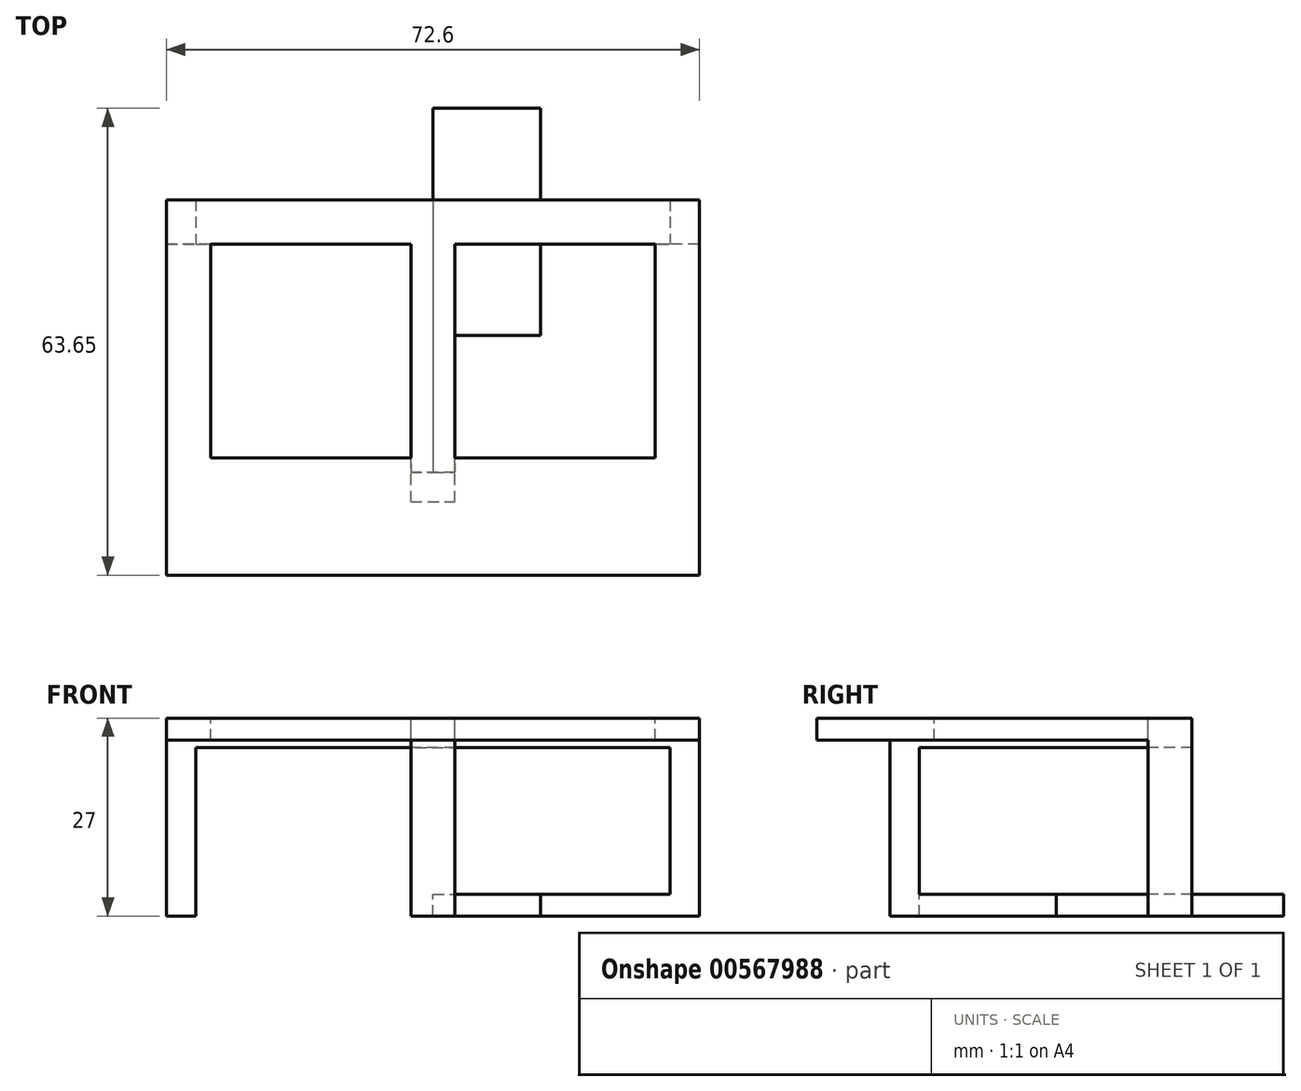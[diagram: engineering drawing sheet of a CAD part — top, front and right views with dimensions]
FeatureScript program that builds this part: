
annotation { "Feature Type Name" : "Feature", "Feature Type Description" : "" }
export const myFeature = defineFeature(function(context is Context, id is Id, definition is map)
    precondition{}
    {
        {
            var Q0;
            Q0=qCreatedBy(makeId("Top.planeOp"),FACE);
            var sketch = newSketch(context, id + "F0", { "sketchPlane" : qUnion([Q0])});
            skLineSegment(sketch, "E0.bottom", {"start": v(-32.12, 30.17) * mm, "end": v(-2.82, 30.17) * mm});
            skLineSegment(sketch, "E0.top", {"start": v(-32.12, -0.83) * mm, "end": v(-2.82, -0.83) * mm});
            skLineSegment(sketch, "E0.left", {"start": v(-32.12, 30.17) * mm, "end": v(-32.12, -0.83) * mm});
            skLineSegment(sketch, "E0.right", {"start": v(-2.82, 30.17) * mm, "end": v(-2.82, -0.83) * mm});
            skSolve(sketch);
        }
        {
            var Q0;
            Q0=makeQuery(id+"F0.imprint","IMPRINT",FACE,{"disambiguationData":[TD([[makeQuery(id+"F0.imprint","IMPRINT",EDGE,{"derivedFrom":sQuery(id+"F0.wireOp",EDGE,"E0.bottom")}),-1.0]])]});
            extrude(context, id + "F1", {"entities" : qUnion([Q0]), "depth" : 3 * mm, "offsetDistance" : 25 * mm});
        }
        {
            var Q0;
            Q0=makeQuery(id+"F1.opExtrude","SWEPT_FACE",FACE,{"disambiguationData":[OSD([sQuery(id+"F0.wireOp",EDGE,"E0.right")])]});
            var sketch = newSketch(context, id + "F2", { "sketchPlane" : qUnion([Q0])});
            skLineSegment(sketch, "E1", {"start": v(17.67, 3) * mm, "end": v(17.67, 0) * mm});
            skLineSegment(sketch, "E2.MirrorCS", {"start": v(11.67, 3) * mm, "end": v(11.67, 0) * mm});
            skLineSegment(sketch, "E3", {"start": v(11.67, 3) * mm, "end": v(17.67, 3) * mm});
            skLineSegment(sketch, "E4", {"start": v(11.67, 0) * mm, "end": v(17.67, 0) * mm});
            skSolve(sketch);
        }
        {
            var Q0;
            Q0=makeQuery(id+"F1.opExtrude","SWEPT_FACE",FACE,{"disambiguationData":[OSD([sQuery(id+"F0.wireOp",EDGE,"E0.left")])]});
            var sketch = newSketch(context, id + "F3", { "sketchPlane" : qUnion([Q0])});
            skLineSegment(sketch, "E5", {"start": v(-17.67, 3) * mm, "end": v(-17.67, 0) * mm});
            skLineSegment(sketch, "E6", {"start": v(-11.67, 3) * mm, "end": v(-11.67, 0) * mm});
            skLineSegment(sketch, "E7", {"start": v(-17.67, 3) * mm, "end": v(-11.67, 3) * mm});
            skLineSegment(sketch, "E8", {"start": v(-17.67, 0) * mm, "end": v(-11.67, 0) * mm});
            skSolve(sketch);
        }
        {
            var Q0;
            Q0=makeQuery(id+"F1.opExtrude","SWEPT_FACE",FACE,{"disambiguationData":[OSD([sQuery(id+"F0.wireOp",EDGE,"E0.top")])]});
            var sketch = newSketch(context, id + "F4", { "sketchPlane" : qUnion([Q0])});
            skLineSegment(sketch, "E9", {"start": v(-20.47, 3) * mm, "end": v(-20.47, 0) * mm});
            skLineSegment(sketch, "E10", {"start": v(-14.47, 3) * mm, "end": v(-14.47, 0) * mm});
            skLineSegment(sketch, "E11", {"start": v(-20.47, 3) * mm, "end": v(-14.47, 3) * mm});
            skLineSegment(sketch, "E12", {"start": v(-20.47, 0) * mm, "end": v(-14.47, 0) * mm});
            skSolve(sketch);
        }
        {
            var Q0;
            Q0=makeQuery(id+"F2.imprint","IMPRINT",FACE,{"disambiguationData":[TD([[makeQuery(id+"F2.imprint","IMPRINT",EDGE,{"derivedFrom":sQuery(id+"F2.wireOp",EDGE,"E1")}),-1.0]])]});
            extrude(context, id + "F5", {"entities" : qUnion([Q0]), "operationType" : NewBodyOperationType.ADD, "depth" : 21.65 * mm, "offsetDistance" : 25 * mm});
        }
        {
            var Q0;
            Q0=makeQuery(id+"F3.imprint","IMPRINT",FACE,{"disambiguationData":[TD([[makeQuery(id+"F3.imprint","IMPRINT",EDGE,{"derivedFrom":sQuery(id+"F3.wireOp",EDGE,"E5")}),1.0]])]});
            extrude(context, id + "F6", {"entities" : qUnion([Q0]), "operationType" : NewBodyOperationType.ADD, "depth" : 21.65 * mm, "offsetDistance" : 25 * mm});
        }
        {
            var Q0;
            Q0=makeQuery(id+"F4.imprint","IMPRINT",FACE,{"disambiguationData":[TD([[makeQuery(id+"F4.imprint","IMPRINT",EDGE,{"derivedFrom":sQuery(id+"F4.wireOp",EDGE,"E9")}),1.0]])]});
            extrude(context, id + "F7", {"entities" : qUnion([Q0]), "operationType" : NewBodyOperationType.ADD, "depth" : 22.65 * mm, "offsetDistance" : 25 * mm});
        }
        {
            var Q0;
            Q0=makeQuery(id+"F7.boolean.opBoolean","MERGE",FACE,{"derivedFrom":[makeQuery(id+"F6.boolean.opBoolean","MERGE",FACE,{"derivedFrom":[makeQuery(id+"F5.boolean.opBoolean","MERGE",FACE,{"derivedFrom":[makeQuery(id+"F1.opExtrude","CAP_FACE",FACE,{"disambiguationData":[OSD([sQuery(id+"F0.wireOp",EDGE,"E0.bottom"),sQuery(id+"F0.wireOp",EDGE,"E0.top"),sQuery(id+"F0.wireOp",EDGE,"E0.left"),sQuery(id+"F0.wireOp",EDGE,"E0.right")])],"isStart":false}),makeQuery(id+"F5.opExtrude","SWEPT_FACE",FACE,{"disambiguationData":[OSD([sQuery(id+"F2.wireOp",EDGE,"E3")])]})]}),makeQuery(id+"F6.opExtrude","SWEPT_FACE",FACE,{"disambiguationData":[OSD([sQuery(id+"F3.wireOp",EDGE,"E7")])]})]}),makeQuery(id+"F7.opExtrude","SWEPT_FACE",FACE,{"disambiguationData":[OSD([sQuery(id+"F4.wireOp",EDGE,"E11")])]})]});
            var sketch = newSketch(context, id + "F8", { "sketchPlane" : qUnion([Q0])});
            skLineSegment(sketch, "E13", {"start": v(-20.47, -19.48) * mm, "end": v(-14.47, -19.48) * mm});
            skLineSegment(sketch, "E14", {"start": v(14.83, 17.67) * mm, "end": v(14.83, 11.67) * mm});
            skLineSegment(sketch, "E15", {"start": v(-49.77, 17.67) * mm, "end": v(-49.77, 11.67) * mm});
            skSolve(sketch);
        }
        {
            var Q0;
            {var subQ0=sQuery(id+"F8.wireOp",EDGE,"E14");Q0=makeQuery(id+"F8.imprint","IMPRINT",FACE,{"disambiguationData":[TD([[makeQuery(id+"F8.imprint","IMPRINT",EDGE,{"derivedFrom":subQ0}),1.0]])]});}
            var Q1;
            {var subQ0=sQuery(id+"F8.wireOp",EDGE,"E13");Q1=makeQuery(id+"F8.imprint","IMPRINT",FACE,{"disambiguationData":[TD([[makeQuery(id+"F8.imprint","IMPRINT",EDGE,{"derivedFrom":subQ0}),-1.0]])]});}
            var Q2;
            {var subQ0=sQuery(id+"F8.wireOp",EDGE,"E15");Q2=makeQuery(id+"F8.imprint","IMPRINT",FACE,{"disambiguationData":[TD([[makeQuery(id+"F8.imprint","IMPRINT",EDGE,{"derivedFrom":subQ0}),-1.0]])]});}
            extrude(context, id + "F9", {"entities" : qUnion([Q0, Q1, Q2]), "operationType" : NewBodyOperationType.ADD, "depth" : 24 * mm, "offsetDistance" : 25 * mm});
        }
        {
            var Q0;
            Q0=makeQuery(id+"F9.opExtrude","SWEPT_FACE",FACE,{"disambiguationData":[OSD([sQuery(id+"F8.wireOp",EDGE,"E14")])]});
            var sketch = newSketch(context, id + "F10", { "sketchPlane" : qUnion([Q0])});
            skLineSegment(sketch, "E16", {"start": v(-17.67, 23) * mm, "end": v(-11.67, 23) * mm});
            skSolve(sketch);
        }
        {
            var Q0;
            Q0=makeQuery(id+"F9.opExtrude","SWEPT_FACE",FACE,{"disambiguationData":[OSD([sQuery(id+"F8.wireOp",EDGE,"E15")])]});
            var sketch = newSketch(context, id + "F11", { "sketchPlane" : qUnion([Q0])});
            skLineSegment(sketch, "E17", {"start": v(17.67, 23) * mm, "end": v(11.67, 23) * mm});
            skSolve(sketch);
        }
        {
            var Q0;
            Q0=makeQuery(id+"F9.opExtrude","SWEPT_FACE",FACE,{"disambiguationData":[OSD([sQuery(id+"F8.wireOp",EDGE,"E13")])]});
            var sketch = newSketch(context, id + "F12", { "sketchPlane" : qUnion([Q0])});
            skLineSegment(sketch, "E18", {"start": v(14.47, 23) * mm, "end": v(20.47, 23) * mm});
            skSolve(sketch);
        }
        {
            var Q0;
            {var subQ0=sQuery(id+"F10.wireOp",EDGE,"E16");Q0=makeQuery(id+"F10.imprint","IMPRINT",FACE,{"disambiguationData":[TD([[makeQuery(id+"F10.imprint","IMPRINT",EDGE,{"derivedFrom":subQ0}),1.0]])]});}
            extrude(context, id + "F13", {"entities" : qUnion([Q0]), "operationType" : NewBodyOperationType.ADD, "depth" : 35.95 * mm, "offsetDistance" : 25 * mm});
        }
        {
            var Q0;
            {var subQ0=sQuery(id+"F11.wireOp",EDGE,"E17");Q0=makeQuery(id+"F11.imprint","IMPRINT",FACE,{"disambiguationData":[TD([[makeQuery(id+"F11.imprint","IMPRINT",EDGE,{"derivedFrom":subQ0}),-1.0]])]});}
            extrude(context, id + "F14", {"entities" : qUnion([Q0]), "operationType" : NewBodyOperationType.ADD, "depth" : 35.95 * mm, "offsetDistance" : 25 * mm});
        }
        {
            var Q0;
            {var subQ0=sQuery(id+"F12.wireOp",EDGE,"E18");Q0=makeQuery(id+"F12.imprint","IMPRINT",FACE,{"disambiguationData":[TD([[makeQuery(id+"F12.imprint","IMPRINT",EDGE,{"derivedFrom":subQ0}),1.0]])]});}
            extrude(context, id + "F15", {"entities" : qUnion([Q0]), "operationType" : NewBodyOperationType.ADD, "depth" : 33.8 * mm, "offsetDistance" : 25 * mm});
        }
        {
            var Q0;
            Q0=makeQuery(id+"F7.boolean.opBoolean","MERGE",FACE,{"derivedFrom":[makeQuery(id+"F6.boolean.opBoolean","MERGE",FACE,{"derivedFrom":[makeQuery(id+"F5.boolean.opBoolean","MERGE",FACE,{"derivedFrom":[makeQuery(id+"F1.opExtrude","CAP_FACE",FACE,{"disambiguationData":[OSD([sQuery(id+"F0.wireOp",EDGE,"E0.bottom"),sQuery(id+"F0.wireOp",EDGE,"E0.top"),sQuery(id+"F0.wireOp",EDGE,"E0.left"),sQuery(id+"F0.wireOp",EDGE,"E0.right")])],"isStart":false}),makeQuery(id+"F5.opExtrude","SWEPT_FACE",FACE,{"disambiguationData":[OSD([sQuery(id+"F2.wireOp",EDGE,"E3")])]})]}),makeQuery(id+"F6.opExtrude","SWEPT_FACE",FACE,{"disambiguationData":[OSD([sQuery(id+"F3.wireOp",EDGE,"E7")])]})]}),makeQuery(id+"F7.opExtrude","SWEPT_FACE",FACE,{"disambiguationData":[OSD([sQuery(id+"F4.wireOp",EDGE,"E11")])]})]});
            var sketch = newSketch(context, id + "F16", { "sketchPlane" : qUnion([Q0])});
            skLineSegment(sketch, "E19", {"start": v(14.83, 14.67) * mm, "end": v(-49.77, 14.67) * mm});
            skLineSegment(sketch, "E20", {"start": v(-17.47, 30.17) * mm, "end": v(-17.47, -19.48) * mm});
            skCircle(sketch, "E21", {"center": v(-17.47, 14.67) * mm, "radius": 1 * mm});
            skSolve(sketch);
        }
        {
            var Q0;
            {var subQ0=sQuery(id+"F16.wireOp",EDGE,"E21");var subQ1=sQuery(id+"F16.wireOp",EDGE,"E19");var subQ2=makeQuery(id+"F16.imprint","INTERSECT",VERTEX,{"disambiguationData":[OD(0.0)],"derivedFrom":[subQ1,subQ0]});Q0=makeQuery(id+"F16.imprint","IMPRINT",FACE,{"disambiguationData":[TD([[makeQuery(id+"F16.imprint","IMPRINT",EDGE,{"disambiguationData":[TD([[subQ2,-1.0]])],"derivedFrom":subQ1}),1.0]])]});}
            var Q1;
            {var subQ0=sQuery(id+"F16.wireOp",EDGE,"E21");var subQ1=sQuery(id+"F16.wireOp",EDGE,"E19");var subQ2=makeQuery(id+"F16.imprint","INTERSECT",VERTEX,{"disambiguationData":[OD(0.0)],"derivedFrom":[subQ1,subQ0]});Q1=makeQuery(id+"F16.imprint","IMPRINT",FACE,{"disambiguationData":[TD([[makeQuery(id+"F16.imprint","IMPRINT",EDGE,{"disambiguationData":[TD([[subQ2,-1.0]])],"derivedFrom":subQ1}),-1.0]])]});}
            var Q2;
            {var subQ0=sQuery(id+"F16.wireOp",EDGE,"E20");var subQ1=sQuery(id+"F16.wireOp",EDGE,"E19");var subQ2=makeQuery(id+"F16.imprint","INTERSECT",VERTEX,{"derivedFrom":[subQ1,subQ0]});Q2=makeQuery(id+"F16.imprint","IMPRINT",FACE,{"disambiguationData":[TD([[makeQuery(id+"F16.imprint","IMPRINT",EDGE,{"disambiguationData":[TD([[subQ2,-1.0]])],"derivedFrom":subQ1}),-1.0]])]});}
            var Q3;
            {var subQ0=sQuery(id+"F16.wireOp",EDGE,"E20");var subQ1=sQuery(id+"F16.wireOp",EDGE,"E19");var subQ2=makeQuery(id+"F16.imprint","INTERSECT",VERTEX,{"derivedFrom":[subQ1,subQ0]});Q3=makeQuery(id+"F16.imprint","IMPRINT",FACE,{"disambiguationData":[TD([[makeQuery(id+"F16.imprint","IMPRINT",EDGE,{"disambiguationData":[TD([[subQ2,-1.0]])],"derivedFrom":subQ1}),1.0]])]});}
            extrude(context, id + "F17", {"entities" : qUnion([Q0, Q1, Q2, Q3]), "operationType" : NewBodyOperationType.REMOVE, "oppositeDirection" : true, "depth" : 4 * mm, "offsetDistance" : 25 * mm});
        }
        {
            var Q0;
            {var subQ0=sQuery(id+"F8.wireOp",EDGE,"E13");var subQ1=sQuery(id+"F8.wireOp",EDGE,"E15");var subQ2=sQuery(id+"F8.wireOp",EDGE,"E14");Q0=makeQuery(id+"F15.boolean.opBoolean","MERGE",FACE,{"derivedFrom":[makeQuery(id+"F9.opExtrude","CAP_FACE",FACE,{"disambiguationData":[OSD([sQuery(id+"F0.wireOp",EDGE,"E0.top"),sQuery(id+"F4.wireOp",EDGE,"E9"),sQuery(id+"F4.wireOp",EDGE,"E10"),sQuery(id+"F4.wireOp",EDGE,"E11"),subQ0])],"isStart":false}),makeQuery(id+"F14.boolean.opBoolean","MERGE",FACE,{"derivedFrom":[makeQuery(id+"F9.opExtrude","CAP_FACE",FACE,{"disambiguationData":[OSD([sQuery(id+"F0.wireOp",EDGE,"E0.left"),sQuery(id+"F3.wireOp",EDGE,"E5"),sQuery(id+"F3.wireOp",EDGE,"E6"),sQuery(id+"F3.wireOp",EDGE,"E7"),subQ1])],"isStart":false}),makeQuery(id+"F13.boolean.opBoolean","MERGE",FACE,{"derivedFrom":[makeQuery(id+"F9.opExtrude","CAP_FACE",FACE,{"disambiguationData":[OSD([sQuery(id+"F0.wireOp",EDGE,"E0.right"),sQuery(id+"F2.wireOp",EDGE,"E1"),sQuery(id+"F2.wireOp",EDGE,"E2.MirrorCS"),sQuery(id+"F2.wireOp",EDGE,"E3"),subQ2])],"isStart":false}),makeQuery(id+"F13.opExtrude","SWEPT_FACE",FACE,{"disambiguationData":[OSD([subQ2])]})]}),makeQuery(id+"F14.opExtrude","SWEPT_FACE",FACE,{"disambiguationData":[OSD([subQ1])]})]}),makeQuery(id+"F15.opExtrude","SWEPT_FACE",FACE,{"disambiguationData":[OSD([subQ0])]})]});}
            var sketch = newSketch(context, id + "F18", { "sketchPlane" : qUnion([Q0])});
            skLineSegment(sketch, "E22", {"start": v(-53.77, 11.67) * mm, "end": v(-53.77, -23.48) * mm});
            skLineSegment(sketch, "E23", {"start": v(-53.77, -23.48) * mm, "end": v(-20.47, -23.48) * mm});
            skLineSegment(sketch, "E24", {"start": v(18.83, 11.67) * mm, "end": v(18.83, -23.48) * mm});
            skLineSegment(sketch, "E25", {"start": v(18.83, -23.48) * mm, "end": v(-14.47, -23.48) * mm});
            skLineSegment(sketch, "E26", {"start": v(18.83, 11.67) * mm, "end": v(12.83, 11.67) * mm});
            skLineSegment(sketch, "E27", {"start": v(12.83, 11.67) * mm, "end": v(12.83, -17.48) * mm});
            skLineSegment(sketch, "E28", {"start": v(-14.47, -23.48) * mm, "end": v(-14.47, -17.48) * mm});
            skLineSegment(sketch, "E29", {"start": v(-14.47, -17.48) * mm, "end": v(12.83, -17.48) * mm});
            skLineSegment(sketch, "E30", {"start": v(-53.77, 11.67) * mm, "end": v(-47.77, 11.67) * mm});
            skLineSegment(sketch, "E31", {"start": v(-20.47, -23.48) * mm, "end": v(-20.47, -17.48) * mm});
            skLineSegment(sketch, "E32", {"start": v(-47.77, 11.67) * mm, "end": v(-47.77, -17.48) * mm});
            skLineSegment(sketch, "E33", {"start": v(-47.77, -17.48) * mm, "end": v(-20.47, -17.48) * mm});
            skSolve(sketch);
        }
        {
            var Q0;
            Q0=makeQuery(id+"F18.imprint","IMPRINT",FACE,{"disambiguationData":[TD([[makeQuery(id+"F18.imprint","IMPRINT",EDGE,{"derivedFrom":sQuery(id+"F18.wireOp",EDGE,"E24")}),-1.0]])]});
            var Q1;
            Q1=makeQuery(id+"F18.imprint","IMPRINT",FACE,{"disambiguationData":[TD([[makeQuery(id+"F18.imprint","IMPRINT",EDGE,{"derivedFrom":sQuery(id+"F18.wireOp",EDGE,"E22")}),1.0]])]});
            extrude(context, id + "F19", {"entities" : qUnion([Q0, Q1]), "operationType" : NewBodyOperationType.ADD, "oppositeDirection" : true, "depth" : 3 * mm, "offsetDistance" : 25 * mm});
        }
        {
            var Q0;
            {var subQ0=sQuery(id+"F4.wireOp",EDGE,"E11");Q0=makeQuery(id+"F19.boolean.opBoolean","MERGE",FACE,{"derivedFrom":[makeQuery(id+"F9.boolean.opBoolean","MERGE",FACE,{"derivedFrom":[makeQuery(id+"F7.opExtrude","CAP_FACE",FACE,{"disambiguationData":[OSD([sQuery(id+"F4.wireOp",EDGE,"E9"),sQuery(id+"F4.wireOp",EDGE,"E10"),subQ0,sQuery(id+"F4.wireOp",EDGE,"E12")])],"isStart":false}),makeQuery(id+"F9.opExtrude","SWEPT_FACE",FACE,{"disambiguationData":[OSD([subQ0])]})]}),makeQuery(id+"F19.opExtrude","SWEPT_FACE",FACE,{"disambiguationData":[OSD([sQuery(id+"F18.wireOp",EDGE,"E23")])]}),makeQuery(id+"F19.opExtrude","SWEPT_FACE",FACE,{"disambiguationData":[OSD([sQuery(id+"F18.wireOp",EDGE,"E25")])]})]});}
            var sketch = newSketch(context, id + "F20", { "sketchPlane" : qUnion([Q0])});
            skLineSegment(sketch, "E34", {"start": v(-20.47, 24) * mm, "end": v(-14.47, 24) * mm});
            skSolve(sketch);
        }
        {
            var Q0;
            Q0=makeQuery(id+"F20.imprint","IMPRINT",FACE,{"disambiguationData":[TD([[makeQuery(id+"F20.imprint","IMPRINT",EDGE,{"derivedFrom":sQuery(id+"F20.wireOp",EDGE,"E34")}),1.0]])]});
            extrude(context, id + "F21", {"entities" : qUnion([Q0]), "operationType" : NewBodyOperationType.ADD, "depth" : 10 * mm, "offsetDistance" : 25 * mm});
        }
    });
